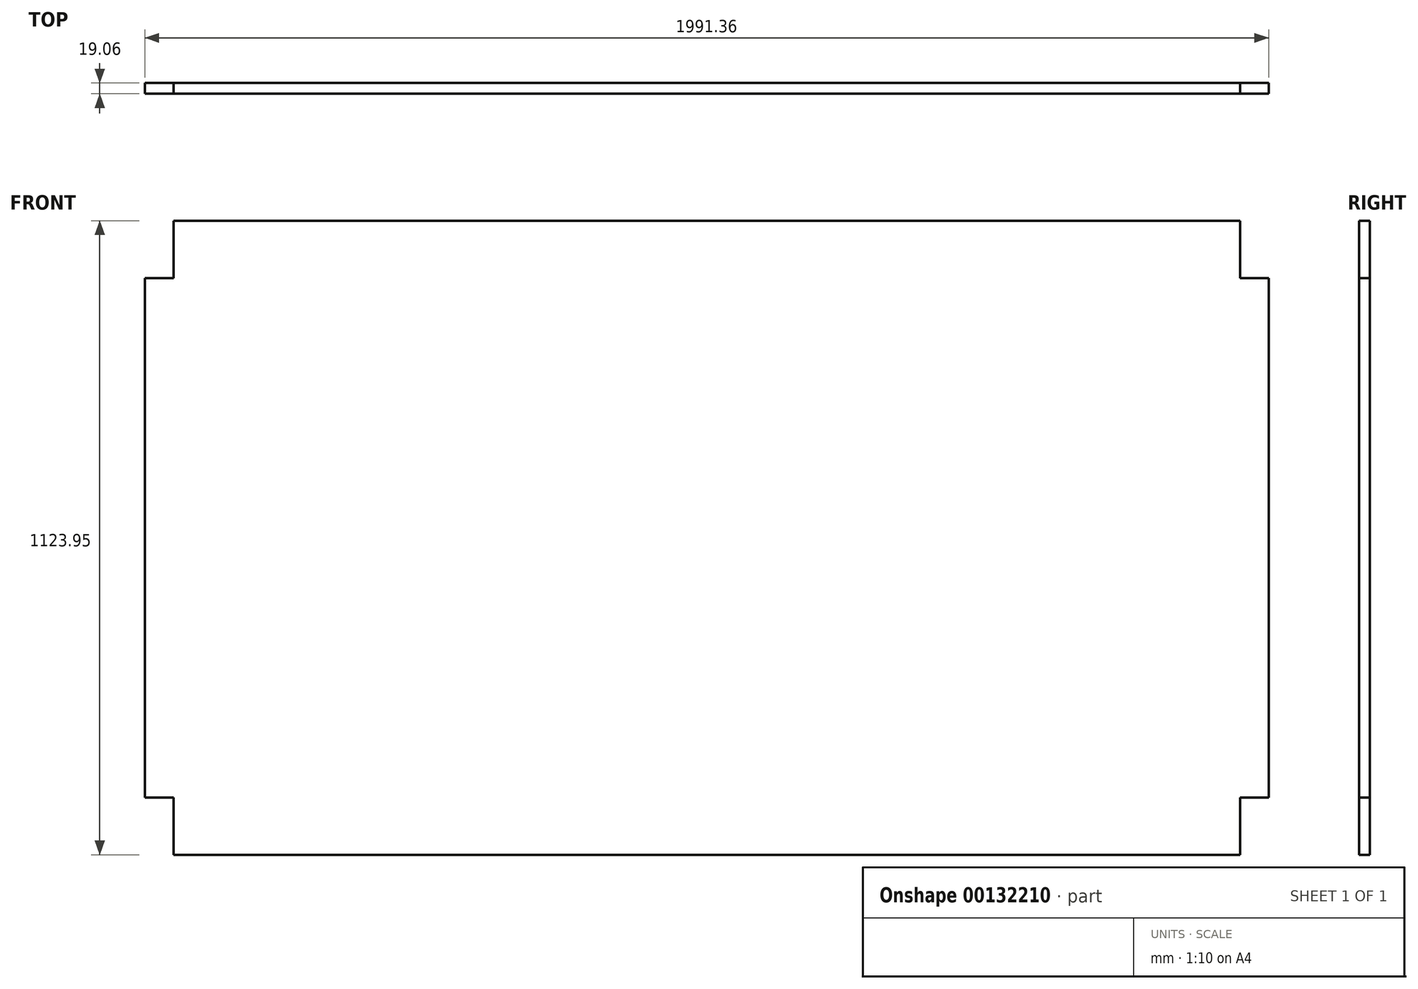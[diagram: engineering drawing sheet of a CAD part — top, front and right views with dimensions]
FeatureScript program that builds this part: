
annotation { "Feature Type Name" : "Feature", "Feature Type Description" : "" }
export const myFeature = defineFeature(function(context is Context, id is Id, definition is map)
    precondition{}
    {
        {
            var Q0;
            Q0=qCreatedBy(makeId("Front.planeOp"),FACE);
            var sketch = newSketch(context, id + "F0", { "sketchPlane" : qUnion([Q0])});
            skLineSegment(sketch, "E0.bottom", {"start": v(944.88, -594.95) * mm, "end": v(-944.88, -594.95) * mm});
            skLineSegment(sketch, "E0.top", {"start": v(944.88, 529) * mm, "end": v(-944.88, 529) * mm});
            skLineSegment(sketch, "E0.left", {"start": v(944.88, -594.95) * mm, "end": v(944.88, -493.35) * mm});
            skLineSegment(sketch, "E0.right", {"start": v(-944.88, -594.95) * mm, "end": v(-944.88, -493.35) * mm});
            skPoint(sketch, "E0.middle", {"position": v(0, -32.97) * mm});
            skPoint(sketch, "E1", {"position": v(-944.88, -493.35) * mm});
            skPoint(sketch, "E2", {"position": v(-995.68, -493.35) * mm});
            skLineSegment(sketch, "E3", {"start": v(-995.68, -493.35) * mm, "end": v(-944.88, -493.35) * mm});
            skLineSegment(sketch, "E4", {"start": v(-995.68, -493.35) * mm, "end": v(-995.68, 427.4) * mm});
            skLineSegment(sketch, "E5", {"start": v(944.88, -493.35) * mm, "end": v(995.68, -493.35) * mm});
            skLineSegment(sketch, "E6", {"start": v(995.68, -493.35) * mm, "end": v(995.68, 427.4) * mm});
            skLineSegment(sketch, "E7", {"start": v(944.88, 529) * mm, "end": v(944.88, 427.4) * mm});
            skLineSegment(sketch, "E8", {"start": v(944.88, 427.4) * mm, "end": v(995.68, 427.4) * mm});
            skLineSegment(sketch, "E9", {"start": v(-944.88, 529) * mm, "end": v(-944.88, 427.4) * mm});
            skLineSegment(sketch, "E10", {"start": v(-944.88, 427.4) * mm, "end": v(-995.68, 427.4) * mm});
            skPoint(sketch, "E11.start.orphan", {"position": v(-995.68, 529) * mm});
            skPoint(sketch, "E12.orphan", {"position": v(995.68, 529) * mm});
            skSolve(sketch);
        }
        {
            var Q0;
            Q0=makeQuery(id+"F0.imprint","IMPRINT",FACE,{"disambiguationData":[TD([[makeQuery(id+"F0.imprint","IMPRINT",EDGE,{"derivedFrom":sQuery(id+"F0.wireOp",EDGE,"E0.bottom")}),-1.0]])]});
            extrude(context, id + "F1", {"entities" : qUnion([Q0]), "endBound" : BoundingType.SYMMETRIC, "depth" : 19.05 * mm});
        }
    });
